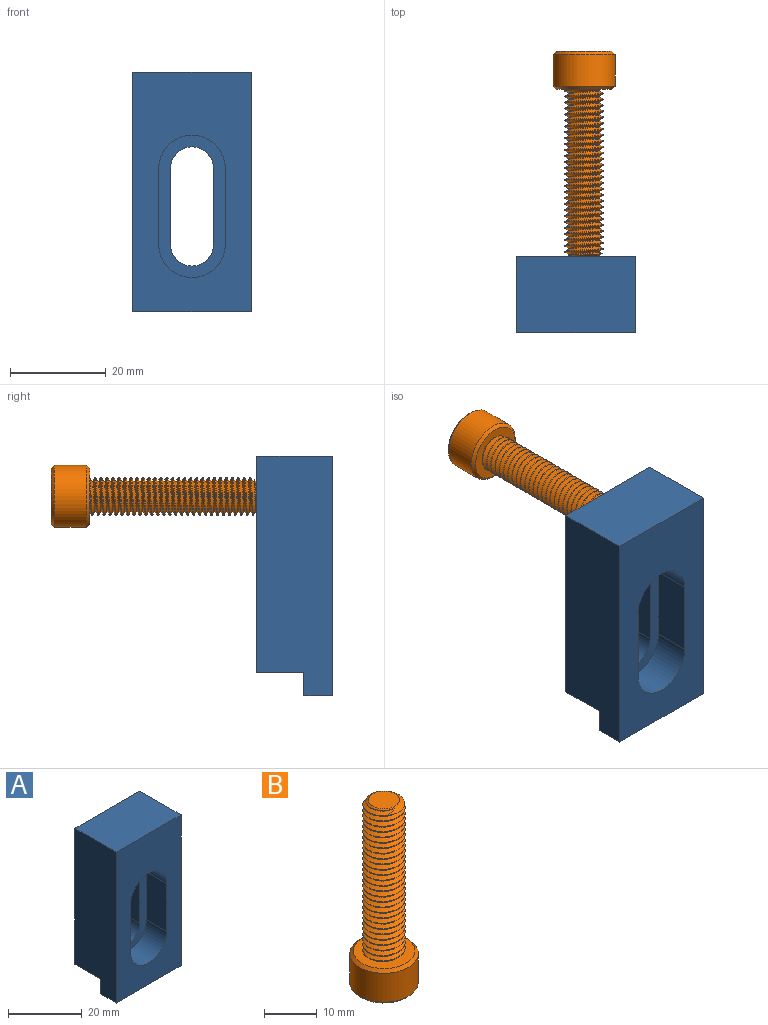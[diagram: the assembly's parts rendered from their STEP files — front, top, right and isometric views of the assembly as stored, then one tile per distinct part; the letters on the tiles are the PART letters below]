
ASSEMBLY  parts=2 mates=1
PART A: 17 faces, bbox 24.9x15.9x50.1 mm
  f0: plane 50.12x24.85mm, normal (0,-1,0), area 872.2mm2, adj f2,f3,f4,f5,f8,f9,f10,f11
  f1: plane 45.2x24.85mm, normal (0,1,0), area 916.1mm2, adj f2,f3,f4,f6,f13,f14,f15,f16
  f2: plane 50.12x15.89mm, normal (-1,0,0), area 747.8mm2, adj f0,f1,f4,f5,f6,f7
  f3: plane 50.12x15.89mm, normal (1,0,0), area 747.8mm2, adj f0,f1,f4,f5,f6,f7
  f4: plane 24.85x15.89mm, normal (0,0,1), area 394.9mm2, adj f0,f1,f2,f3
  f5: plane 24.85x6.02mm, normal (0,0,-1), area 149.6mm2, adj f0,f2,f3,f7
  f6: plane 24.85x9.87mm, normal (0,0,-1), area 245.3mm2, adj f1,f2,f3,f7
  f7: plane 24.85x4.92mm, normal (0,1,0), area 122.3mm2, adj f2,f3,f5,f6
  f8: plane 15.94x7.88mm, normal (-1,0,0), area 125.6mm2, adj f0,f9,f11,f12
  f9: cylinder r=6.95mm len=13.9mm, axis (0,-1,0), area 172.1mm2, adj f0,f8,f10,f12
  f10: plane 15.94x7.88mm, normal (1,0,0), area 125.6mm2, adj f0,f9,f11,f12
  f11: cylinder r=6.95mm len=13.9mm, axis (0,-1,0), area 172.1mm2, adj f0,f8,f10,f12
  f12: plane 29.84x13.9mm, normal (0,-1,0), area 166.2mm2, adj f8,f9,f10,f11,f13,f14,f15,f16
  f13: cylinder r=4.5mm len=9mm, axis (0,-1,0), area 113.2mm2, adj f1,f12,f14,f16
  f14: plane 15.94x8.01mm, normal (-1,0,0), area 127.7mm2, adj f1,f12,f13,f15
  f15: cylinder r=4.5mm len=9mm, axis (0,-1,0), area 113.2mm2, adj f1,f12,f14,f16
  f16: plane 15.94x8.01mm, normal (1,0,0), area 127.7mm2, adj f1,f12,f13,f15
PART B: 24 faces, bbox 13.5x13.5x43.8 mm
  f0: cone r=6.5mm half-angle=45deg, axis (0,0,-1), area 35.7mm2, adj f3,f11
  f1: cone r=5.85mm half-angle=45deg, axis (0,0,1), area 35.7mm2, adj f3,f10
  f2: cone r=3.46mm half-angle=45deg, axis (0,0,-1), area 1.1mm2, adj f10,f22
  f3: cylinder r=6.5mm len=13mm, axis (0,0,1), area 273.6mm2, adj f0,f1
  f4: cone r=2.93mm half-angle=55deg, axis (0,0,-1), area 16.9mm2, adj f5,f6,f7,f8,f9
  f5: cylinder r=3.19mm len=34.82mm, axis (0,0,-1), area 87.2mm2, adj f4,f7,f8,f11
  f6: cylinder r=4mm len=34.25mm, axis (0,0,1), area 107.6mm2, adj f4,f7,f8,f11
  f7: bspline ~35.76x8mm, area 587.6mm2, adj f4,f5,f6,f11
  f8: bspline ~35.29x8mm, area 585.4mm2, adj f4,f5,f6,f11
  f9: plane 5.87x5.87mm, normal (0,0,1), area 27mm2, adj f4
  f10: plane 11.7x11.7mm, normal (0,0,-1), area 69.8mm2, adj f1,f2,f12,f13,f14,f15,f16
  f11: plane 12.2x12.2mm, normal (0,0,1), area 66.7mm2, adj f0,f5,f6,f7,f8
  f12: cone r=3.46mm half-angle=45deg, axis (0,0,-1), area 1.5mm2, adj f10,f18
  f13: cone r=3.46mm half-angle=45deg, axis (0,0,-1), area 1.5mm2, adj f10,f19
  f14: cone r=3.46mm half-angle=45deg, axis (0,0,-1), area 1.5mm2, adj f10,f20
  f15: cone r=3.46mm half-angle=45deg, axis (0,0,-1), area 1.5mm2, adj f10,f21
  f16: cone r=3.46mm half-angle=45deg, axis (0,0,-1), area 1.5mm2, adj f10,f23
  f17: plane 6.93x6mm, normal (0,0,-1), area 31.2mm2, adj f18,f19,f20,f21,f22,f23
  f18: plane 4.5x3mm, normal (-0.5,-0.87,0), area 14.5mm2, adj f12,f17,f19,f23
  f19: plane 4.5x3.46mm, normal (-1,0,0), area 14.5mm2, adj f13,f17,f18,f20
  f20: plane 4.5x3mm, normal (-0.5,0.87,0), area 14.5mm2, adj f14,f17,f19,f21
  f21: plane 4.5x3mm, normal (0.5,0.87,0), area 14.5mm2, adj f15,f17,f20,f22
  f22: plane 4.84x3.8mm, normal (1,0,0), area 14.5mm2, adj f2,f17,f21,f23
  f23: plane 4.5x3mm, normal (0.5,-0.87,0), area 14.5mm2, adj f16,f17,f18,f22
PLACE A t=(-29.3,-8.31,-4.31)mm
PLACE B rot(axis=(1,0,0),90deg) t=(-15.2,7.58,37.41)mm
MATE planar B.f0 <-> A.f1  axis (0,-1,0) through (-15.2,7.58,37.41)mm
